# Revit family: AS_E_2607_OS275
name_source: partatom
category: Porte
units: mm (PartAtom-declared; Revit-internal decimal feet)

## family parameters
Condiviso = No
Host = Muro
Numero OmniClass = 23.30.10.00
Punto di calcolo locali = Sì
Sempre verticale = Sì
Taglio con vuoti quando caricato = Sì
Titolo OmniClass = Doors

## types (4) — shared parameters
Altezza = 3000 mm  [stored 9.84252 ft]
Altezza_ante = 2927 mm
Chiusura muro = Per host
Costruzione analitica = <Nessuno>
Descrizione = Alzante scorrevole 4 ante, 2 ante mobili
Funzione = Interno
H = 3000 mm  [stored 9.84252 ft]
H1 = 3000 mm  [stored 9.84252 ft]
H_Max = 3000 mm  [stored 9.84252 ft]
H_Min = 1230 mm
H_man = 996 mm
H_maniglia = 996 mm
H_vetro = 2851 mm  [stored 9.35367 ft]
L = 3370 mm  [stored 11.0564 ft]
L1 = 3370 mm  [stored 11.0564 ft]
L_Max = 6200 mm
L_Min = 3370 mm  [stored 11.0564 ft]
L_vetro = 771 mm
Larghezza = 3000 mm  [stored 9.84252 ft]
Larghezza telaio = 75 mm
Larghezza_1A = 847 mm
Larghezza_2A = 847 mm
Maniglia_alta = 996 mm
Maniglia_bassa = 396 mm
Modello = OS2 75 AS
Produttore = Secco Sistemi Spa
Proiezione telaio est. = 25 mm  [stored 0.082021 ft]
Proiezione telaio int. = 25 mm  [stored 0.082021 ft]
URL = https://www.seccosistemi.com
WARNING = Sì

## per-type parameters (varying)
| type | MATERIALE |
| Acciaio zincato | Acciaio |
| Acciaio inox | Acciaio inox, spazzolato |
| Ottone | Ottone |
| Acciaio Corten | Acciaio corten |

note: [stored X ft] marks values corroborated as IEEE doubles in the binary element streams (Revit-internal decimal feet)
